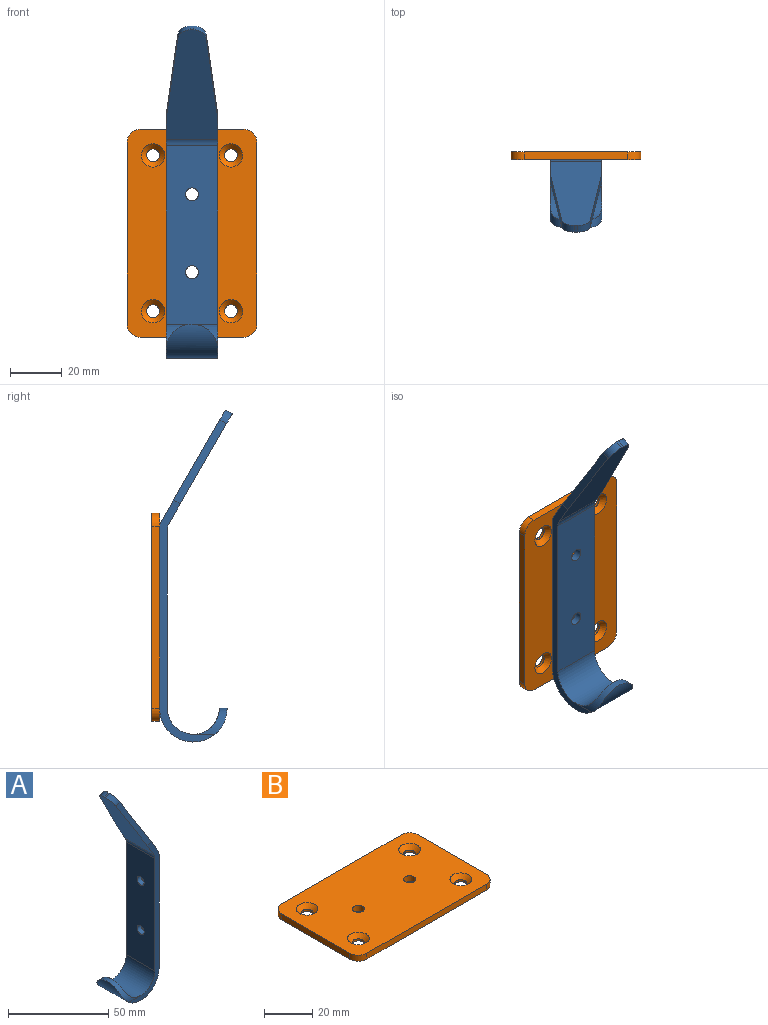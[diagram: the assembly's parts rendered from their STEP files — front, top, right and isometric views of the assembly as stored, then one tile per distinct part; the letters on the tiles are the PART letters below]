
ASSEMBLY  parts=2 mates=1
PART A: 18 faces, bbox 28x20x127.8 mm
  f0: cylinder r=13mm len=26mm, axis (0,1,0), area 772.6mm2, adj f1,f7,f8,f9
  f1: plane 69.46x20mm, normal (1,0,0), area 1350mm2, adj f0,f7,f8,f14,f15,f16
  f2: plane 42.84x24.73mm, normal (0.87,0,0.5), area 781.3mm2, adj f3,f7,f8,f10,f11,f12,f13,f16
  f3: plane 2.6x1.5mm, normal (-0.5,0,0.87), area 3.5mm2, adj f2,f4,f12,f13
  f4: plane 42.14x24.33mm, normal (-0.87,0,-0.5), area 765.2mm2, adj f3,f7,f8,f10,f11,f12,f13,f17
  f5: plane 68.66x20mm, normal (-1,0,0), area 1333.9mm2, adj f6,f7,f8,f14,f15,f17
  f6: cylinder r=10mm len=20mm, axis (0,1,0), area 582.9mm2, adj f5,f7,f8,f9
  f7: plane 93.16x21.31mm, normal (0,-1,0), area 313.6mm2, adj f0,f1,f2,f4,f5,f6,f9,f10
  f8: plane 93.16x21.31mm, normal (0,1,0), area 313.6mm2, adj f0,f1,f2,f4,f5,f6,f9,f11
  f9: cylinder r=10mm len=20mm, axis (1,0,0), area 109.2mm2, adj f0,f6,f7,f8
  f10: plane 32.35x20.41mm, normal (-0.06,-0.99,0.11), area 107.7mm2, adj f2,f4,f7,f12
  f11: plane 32.35x20.41mm, normal (-0.06,0.99,0.11), area 107.7mm2, adj f2,f4,f8,f13
  f12: cylinder r=5mm len=5.29mm, axis (-0.87,0,-0.5), area 21.7mm2, adj f2,f3,f4,f10
  f13: cylinder r=5mm len=5.29mm, axis (-0.87,0,-0.5), area 21.7mm2, adj f2,f3,f4,f11
  f14: cylinder r=2.5mm len=5mm, axis (-1,0,0), area 47.1mm2, adj f1,f5
  f15: cylinder r=2.5mm len=5mm, axis (-1,0,0), area 47.1mm2, adj f1,f5
  f16: cylinder r=5mm len=20mm, axis (0,1,0), area 52.4mm2, adj f1,f2,f7,f8
  f17: cylinder r=5mm len=20mm, axis (0,-1,0), area 52.4mm2, adj f4,f5,f7,f8
PART B: 20 faces, bbox 80x50x3 mm
  f0: plane 70x3mm, normal (0,-1,0), area 210mm2, adj f4,f5,f6,f9
  f1: plane 40x3mm, normal (1,0,0), area 120mm2, adj f4,f5,f6,f7
  f2: plane 70x3mm, normal (0,1,0), area 210mm2, adj f4,f5,f7,f8
  f3: plane 40x3mm, normal (-1,0,0), area 120mm2, adj f4,f5,f8,f9
  f4: plane 80x50mm, normal (0,0,1), area 3684.8mm2, adj f0,f1,f2,f3,f6,f7,f8,f9
  f5: plane 80x50mm, normal (0,0,-1), area 3860.7mm2, adj f0,f1,f2,f3,f6,f7,f8,f9
  f6: cylinder r=5mm len=5mm, axis (0,0,1), area 23.6mm2, adj f0,f1,f4,f5
  f7: cylinder r=5mm len=5mm, axis (0,0,-1), area 23.6mm2, adj f1,f2,f4,f5
  f8: cylinder r=5mm len=5mm, axis (0,0,1), area 23.6mm2, adj f2,f3,f4,f5
  f9: cylinder r=5mm len=5mm, axis (0,0,-1), area 23.6mm2, adj f0,f3,f4,f5
  f10: cylinder r=2.5mm len=5mm, axis (0,0,1), area 15.7mm2, adj f5,f17
  f11: cylinder r=2.5mm len=5mm, axis (0,0,1), area 15.7mm2, adj f5,f15
  f12: cylinder r=2.5mm len=5mm, axis (0,0,1), area 15.7mm2, adj f5,f16
  f13: cylinder r=2.5mm len=5mm, axis (0,0,1), area 15.7mm2, adj f5,f14
  f14: cone r=2.5mm half-angle=45deg, axis (0,0,1), area 62.2mm2, adj f4,f13
  f15: cone r=2.5mm half-angle=45deg, axis (0,0,1), area 62.2mm2, adj f4,f11
  f16: cone r=2.5mm half-angle=45deg, axis (0,0,1), area 62.2mm2, adj f4,f12
  f17: cone r=2.5mm half-angle=45deg, axis (0,0,1), area 62.2mm2, adj f4,f10
  f18: cylinder r=2.5mm len=5mm, axis (0,0,1), area 47.1mm2, adj f4,f5
  f19: cylinder r=2.5mm len=5mm, axis (0,0,1), area 47.1mm2, adj f4,f5
PLACE A rot(axis=(0,0,1),90deg) t=(34.25,-36.48,-40.15)mm
PLACE B rot(axis=(0.58,-0.58,0.58),120deg) t=(69.25,-20.48,34.85)mm
MATE fastened A.f15 <-> B.f18  axis (0,1,0) through (44.25,-23.48,9.85)mm
